# Revit family: Shower-Bath_Shower-STERLING-Accord-71150125_1
name_source: partatom
category: Plumbing Fixtures
revit_build: Autodesk Revit 2015 (Build: 20140606_1530(x64)
units: mm (PartAtom-declared; Revit-internal decimal feet)

## types (2) — shared parameters
ADA Compliant = Yes
Assembly Code = D2010500
CW Connection = No
Cold Water Inlet = Cold Water Inlet
Date Modified = 07/22/2019
Default Elevation = 0"
Description = Series 7115, 60 inch x 32 inch ADA Bath/Shower With Grab Bars and Bath Seat
Drain Included = No
Grab Bar Material = Sterling-Metal-NA-Stainless
HW Connection = No
Height = 75 1/2"
Hot Water Inlet = Hot Water Inlet
Length = 60"
Manufacturer = KOHLER Co.
MasterFormat 1995 = 15410
MasterFormat 2004 = 22.41.19
Material = Vikrell
Product Documentation Link = https://resources.kohler.com
Product Name = Accord
Product Page URL = https://www.sterlingplumbing.com
URL = https://www.sterlingplumbing.com
Vent Connection = No
Waste Connection = Yes
Waste Water Outlet = Waste Water Outlet
WaterSense Certified = No
Width = 33 1/4"

## per-type parameters (varying)
| type | Finish | Model | Type |
| 0-White | Sterling-Vikrell-0-White | 71150125-0 | 1 |
| 96-Biscuit | Sterling-Vikrell-96-Biscuit | 71150125-96 | 2 |

## geometry (parser evidence)
native form markers: Sweep x4
no freeform markers — native parametric forms only
